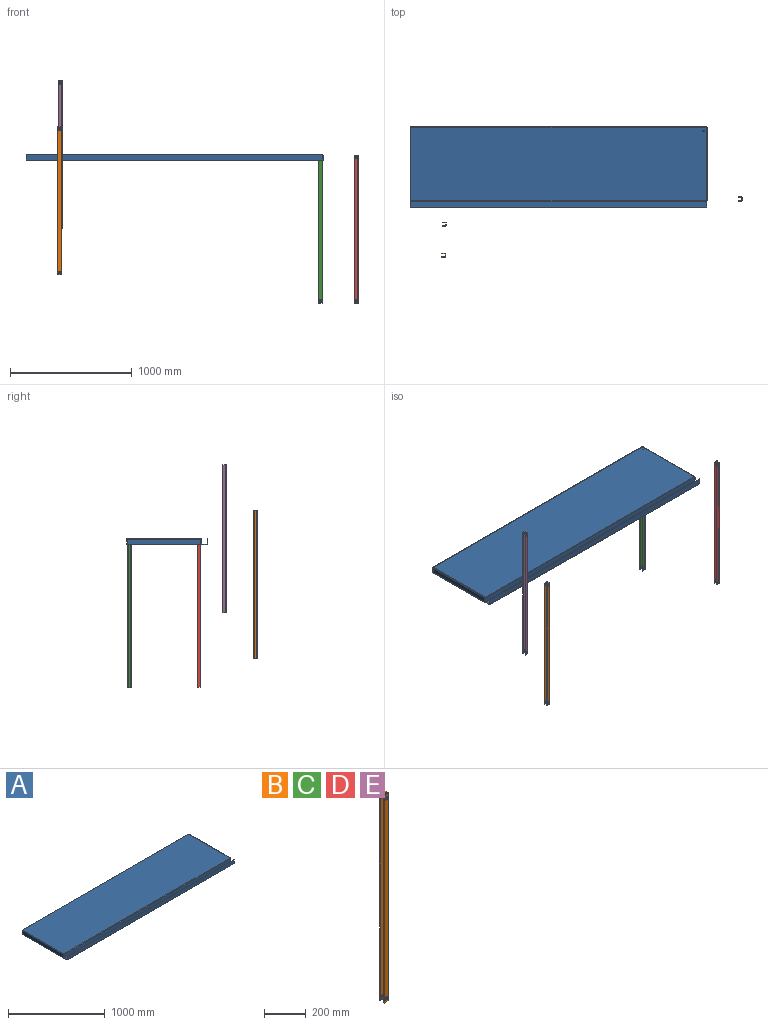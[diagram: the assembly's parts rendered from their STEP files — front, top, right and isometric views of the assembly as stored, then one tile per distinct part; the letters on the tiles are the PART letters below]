
ASSEMBLY  parts=5 mates=2
PART A: 58 faces, bbox 2444.8x666.8x52.1 mm
  f0: plane 605.6x3.18mm, normal (0,0,-1), area 1922.8mm2, adj f1,f2,f3,f4
  f1: plane 45.63x3.18mm, normal (0,1,0), area 144.9mm2, adj f0,f3,f4,f5
  f2: plane 45.63x3.18mm, normal (0,-1,0), area 144.9mm2, adj f0,f3,f4,f6
  f3: plane 605.6x45.63mm, normal (1,0,0), area 27630.5mm2, adj f0,f1,f2,f8
  f4: plane 605.6x45.63mm, normal (-1,0,0), area 27630.5mm2, adj f0,f1,f2,f7
  f5: plane 5.18x5.18mm, normal (0,1,0), area 17.9mm2, adj f1,f7,f8,f27
  f6: plane 5.18x5.18mm, normal (0,-1,0), area 17.9mm2, adj f2,f7,f8,f38
  f7: cylinder r=5.17mm len=605.6mm, axis (0,1,0), area 4922.8mm2, adj f4,f5,f6,f10
  f8: cylinder r=2mm len=605.6mm, axis (0,1,0), area 1902.5mm2, adj f3,f5,f6,f9
  f9: plane 2434.4x605.6mm, normal (0,0,-1), area 1474272.6mm2, adj f8,f19,f30,f40
  f10: plane 2434.4x605.6mm, normal (0,0,1), area 1474272.6mm2, adj f7,f18,f29,f39
  f11: plane 605.6x3.18mm, normal (0,0,-1), area 1922.8mm2, adj f12,f13,f14,f15
  f12: plane 45.63x3.18mm, normal (0,-1,0), area 144.9mm2, adj f11,f14,f15,f16
  f13: plane 45.63x3.18mm, normal (0,1,0), area 144.9mm2, adj f11,f14,f15,f17
  f14: plane 605.6x45.63mm, normal (-1,0,0), area 27630.5mm2, adj f11,f12,f13,f19
  f15: plane 605.6x45.63mm, normal (1,0,0), area 27630.5mm2, adj f11,f12,f13,f18
  f16: plane 5.18x5.18mm, normal (0,-1,0), area 17.9mm2, adj f12,f18,f19,f37
  f17: plane 5.18x5.18mm, normal (0,1,0), area 17.9mm2, adj f13,f18,f19,f28
  f18: cylinder r=5.17mm len=605.6mm, axis (0,-1,0), area 4922.8mm2, adj f10,f15,f16,f17
  f19: cylinder r=2mm len=605.6mm, axis (0,-1,0), area 1902.5mm2, adj f9,f14,f16,f17
  f20: plane 3.18x2mm, normal (0,0,1), area 6.3mm2, adj f24,f25,f26,f27
  f21: plane 2438.4x3.18mm, normal (0,0,-1), area 7741.9mm2, adj f22,f24,f25,f26
  f22: plane 41.13x3.18mm, normal (1,0,0), area 130.6mm2, adj f21,f23,f25,f26
  f23: plane 3.18x2mm, normal (0,0,1), area 6.4mm2, adj f22,f25,f26,f28
  f24: plane 41.13x3.18mm, normal (-1,0,0), area 130.6mm2, adj f20,f21,f25,f26
  f25: plane 2438.4x41.13mm, normal (0,-1,0), area 100289.4mm2, adj f20,f21,f22,f23,f24,f30
  f26: plane 2438.4x41.13mm, normal (0,1,0), area 100289.4mm2, adj f20,f21,f22,f23,f24,f29
  f27: plane 5.18x5.18mm, normal (-1,0,0), area 17.9mm2, adj f5,f20,f29,f30
  f28: plane 5.18x5.18mm, normal (1,0,0), area 17.9mm2, adj f17,f23,f29,f30
  f29: cylinder r=5.17mm len=2434.4mm, axis (-1,0,0), area 19788.9mm2, adj f10,f26,f27,f28
  f30: cylinder r=2mm len=2434.4mm, axis (-1,0,0), area 7647.9mm2, adj f9,f25,f27,f28
  f31: plane 3.18x2mm, normal (0,0,1), area 6.4mm2, adj f34,f35,f36,f37
  f32: plane 39.13x3.18mm, normal (-1,0,0), area 124.2mm2, adj f33,f35,f36,f42
  f33: plane 3.18x2mm, normal (0,0,1), area 6.4mm2, adj f32,f35,f36,f38
  f34: plane 39.13x3.18mm, normal (1,0,0), area 124.2mm2, adj f31,f35,f36,f41
  f35: plane 2438.4x39.13mm, normal (0,1,0), area 95412.6mm2, adj f31,f32,f33,f34,f40,f43
  f36: plane 2438.4x39.13mm, normal (0,-1,0), area 95412.6mm2, adj f31,f32,f33,f34,f39,f44
  f37: plane 5.18x5.18mm, normal (1,0,0), area 17.9mm2, adj f16,f31,f39,f40
  f38: plane 5.18x5.18mm, normal (-1,0,0), area 17.9mm2, adj f6,f33,f39,f40
  f39: cylinder r=5.17mm len=2434.4mm, axis (1,0,0), area 19788.9mm2, adj f10,f36,f37,f38
  f40: cylinder r=2mm len=2434.4mm, axis (1,0,0), area 7647.9mm2, adj f9,f35,f37,f38
  f41: plane 5.18x5.18mm, normal (1,0,0), area 17.9mm2, adj f34,f43,f44,f46
  f42: plane 5.18x5.18mm, normal (-1,0,0), area 17.9mm2, adj f32,f43,f44,f45
  f43: cylinder r=5.17mm len=2438.4mm, axis (1,0,0), area 19821.4mm2, adj f35,f41,f42,f47
  f44: cylinder r=2mm len=2438.4mm, axis (1,0,0), area 7660.5mm2, adj f36,f41,f42,f48
  f45: plane 43.63x3.18mm, normal (-1,0,0), area 138.5mm2, adj f42,f47,f48,f50
  f46: plane 43.63x3.18mm, normal (1,0,0), area 138.5mm2, adj f41,f47,f48,f49
  f47: plane 2438.4x43.63mm, normal (0,0,-1), area 106375.2mm2, adj f43,f45,f46,f51
  f48: plane 2438.4x43.63mm, normal (0,0,1), area 106375.2mm2, adj f44,f45,f46,f52
  f49: plane 5.18x5.18mm, normal (1,0,0), area 17.9mm2, adj f46,f51,f52,f55
  f50: plane 5.18x5.18mm, normal (-1,0,0), area 17.9mm2, adj f45,f51,f52,f54
  f51: cylinder r=5.17mm len=2438.4mm, axis (1,0,0), area 19821.4mm2, adj f47,f49,f50,f56
  f52: cylinder r=2mm len=2438.4mm, axis (1,0,0), area 7660.5mm2, adj f48,f49,f50,f57
  f53: plane 2438.4x3.18mm, normal (0,0,1), area 7741.9mm2, adj f54,f55,f56,f57
  f54: plane 45.63x3.18mm, normal (-1,0,0), area 144.9mm2, adj f50,f53,f56,f57
  f55: plane 45.63x3.18mm, normal (1,0,0), area 144.9mm2, adj f49,f53,f56,f57
  f56: plane 2438.4x45.63mm, normal (0,-1,0), area 111252mm2, adj f51,f53,f54,f55
  f57: plane 2438.4x45.63mm, normal (0,1,0), area 111252mm2, adj f52,f53,f54,f55
PART B: 38 faces, bbox 31.8x31.8x1219.2 mm
  f0: plane 21.4x3.18mm, normal (0,0,1), area 67.9mm2, adj f2,f3,f18,f35
  f1: plane 21.4x3.18mm, normal (0,0,-1), area 67.9mm2, adj f2,f3,f17,f34
  f2: plane 1219.2x21.4mm, normal (-1,0,0), area 26090.9mm2, adj f0,f1,f20,f37
  f3: plane 1219.2x21.4mm, normal (1,0,0), area 26090.9mm2, adj f0,f1,f19,f36
  f4: plane 26.58x3.18mm, normal (0,0,1), area 84.4mm2, adj f14,f15,f16,f18
  f5: plane 26.58x3.18mm, normal (0,0,-1), area 84.4mm2, adj f14,f15,f16,f17
  f6: cylinder r=3.38mm len=6.76mm, axis (0,1,0), area 67.4mm2, adj f15,f16
  f7: cylinder r=3.38mm len=6.76mm, axis (0,1,0), area 67.4mm2, adj f15,f16
  f8: cylinder r=3.38mm len=6.76mm, axis (0,1,0), area 67.4mm2, adj f15,f16
  f9: cylinder r=3.38mm len=6.76mm, axis (0,1,0), area 67.4mm2, adj f15,f16
  f10: cylinder r=3.38mm len=6.76mm, axis (0,1,0), area 67.4mm2, adj f15,f16
  f11: cylinder r=3.38mm len=6.76mm, axis (0,1,0), area 67.4mm2, adj f15,f16
  f12: cylinder r=3.38mm len=6.76mm, axis (0,1,0), area 67.4mm2, adj f15,f16
  f13: cylinder r=3.38mm len=6.76mm, axis (0,1,0), area 67.4mm2, adj f15,f16
  f14: plane 1219.2x3.18mm, normal (-1,0,0), area 3871mm2, adj f4,f5,f15,f16
  f15: plane 1219.2x26.58mm, normal (0,1,0), area 32113.1mm2, adj f4,f5,f6,f7,f8,f9,f10,f11
  f16: plane 1219.2x26.58mm, normal (0,-1,0), area 32113.1mm2, adj f4,f5,f6,f7,f8,f9,f10,f11
  f17: plane 5.18x5.18mm, normal (0,0,-1), area 17.9mm2, adj f1,f5,f19,f20
  f18: plane 5.18x5.18mm, normal (0,0,1), area 17.9mm2, adj f0,f4,f19,f20
  f19: cylinder r=5.17mm len=1219.2mm, axis (0,0,-1), area 9910.7mm2, adj f3,f16,f17,f18
  f20: cylinder r=2mm len=1219.2mm, axis (0,0,-1), area 3830.2mm2, adj f2,f15,f17,f18
  f21: plane 26.58x3.18mm, normal (0,0,1), area 84.4mm2, adj f22,f32,f33,f35
  f22: plane 1219.2x3.18mm, normal (-1,0,0), area 3871mm2, adj f21,f23,f32,f33
  f23: plane 26.58x3.18mm, normal (0,0,-1), area 84.4mm2, adj f22,f32,f33,f34
  f24: cylinder r=3.38mm len=6.76mm, axis (0,-1,0), area 67.4mm2, adj f32,f33
  f25: cylinder r=3.38mm len=6.76mm, axis (0,-1,0), area 67.4mm2, adj f32,f33
  f26: cylinder r=3.38mm len=6.76mm, axis (0,-1,0), area 67.4mm2, adj f32,f33
  f27: cylinder r=3.38mm len=6.76mm, axis (0,-1,0), area 67.4mm2, adj f32,f33
  f28: cylinder r=3.38mm len=6.76mm, axis (0,-1,0), area 67.4mm2, adj f32,f33
  f29: cylinder r=3.38mm len=6.76mm, axis (0,-1,0), area 67.4mm2, adj f32,f33
  f30: cylinder r=3.38mm len=6.76mm, axis (0,-1,0), area 67.4mm2, adj f32,f33
  f31: cylinder r=3.38mm len=6.76mm, axis (0,-1,0), area 67.4mm2, adj f32,f33
  f32: plane 1219.2x26.58mm, normal (0,-1,0), area 32113.1mm2, adj f21,f22,f23,f24,f25,f26,f27,f28
  f33: plane 1219.2x26.58mm, normal (0,1,0), area 32113.1mm2, adj f21,f22,f23,f24,f25,f26,f27,f28
  f34: plane 5.18x5.18mm, normal (0,0,-1), area 17.9mm2, adj f1,f23,f36,f37
  f35: plane 5.18x5.18mm, normal (0,0,1), area 17.9mm2, adj f0,f21,f36,f37
  f36: cylinder r=5.17mm len=1219.2mm, axis (0,0,-1), area 9910.7mm2, adj f3,f33,f34,f35
  f37: cylinder r=2mm len=1219.2mm, axis (0,0,-1), area 3830.2mm2, adj f2,f32,f34,f35
PART C: same geometry as B
PART D: same geometry as B
PART E: same geometry as B
PLACE A t=(16.8,548.31,278.58)mm
PLACE B t=(307.73,87.27,479.81)mm
PLACE C t=(2455.2,1122.99,244.87)mm
PLACE D t=(2746.13,551.05,245.3)mm
PLACE E t=(310.92,342.72,860.22)mm
MATE parallel C.f3 <-> A.f14  axis (1,0,0) through (2455.2,1138.86,-332.98)mm
MATE parallel D.f3 <-> A.f14  axis (1,0,0) through (2746.13,566.92,277.05)mm
